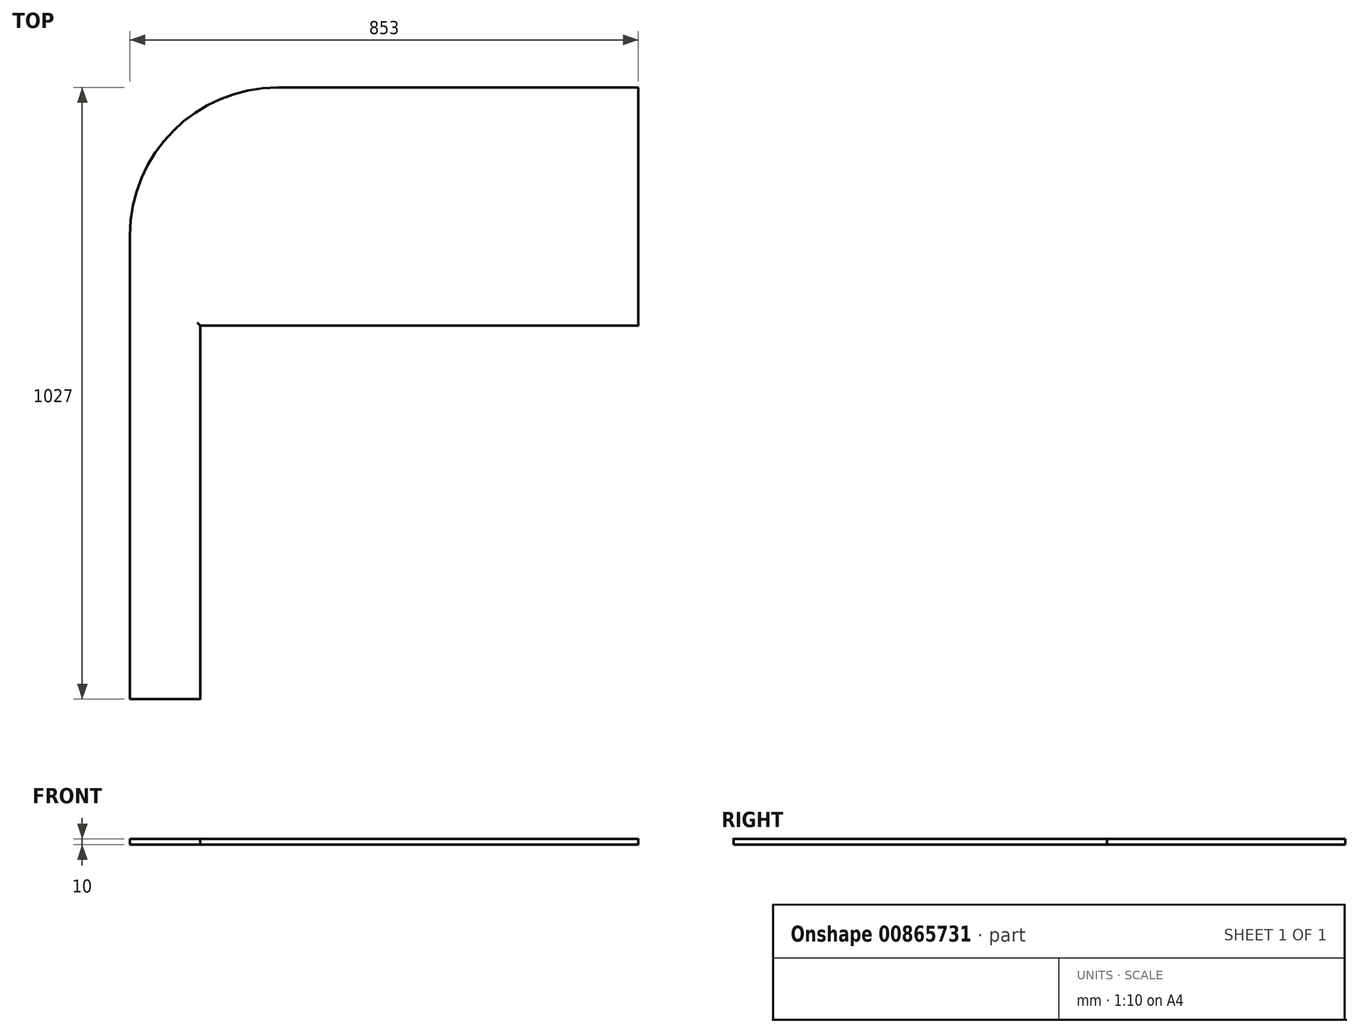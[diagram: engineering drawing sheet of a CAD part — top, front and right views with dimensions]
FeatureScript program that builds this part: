
annotation { "Feature Type Name" : "Feature", "Feature Type Description" : "" }
export const myFeature = defineFeature(function(context is Context, id is Id, definition is map)
    precondition{}
    {
        {
            var Q0;
            Q0=qCreatedBy(makeId("Top.planeOp"),FACE);
            var sketch = newSketch(context, id + "F0", { "sketchPlane" : qUnion([Q0])});
            skLineSegment(sketch, "E0", {"start": v(-248, 0) * mm, "end": v(-248, -779) * mm});
            skLineSegment(sketch, "E1", {"start": v(0, 248) * mm, "end": v(605, 248) * mm});
            skArc(sketch, "E2", {"start": v(0, 248) * mm, "mid": v(-175.36, 175.36) * mm, "end": v(-248, 0) * mm});
            skLineSegment(sketch, "E3", {"start": v(-248, -779) * mm, "end": v(-130, -779) * mm});
            skLineSegment(sketch, "E4", {"start": v(605, 248) * mm, "end": v(605, -152) * mm});
            skLineSegment(sketch, "E5", {"start": v(605, -152) * mm, "end": v(-130, -152) * mm});
            skLineSegment(sketch, "E6", {"start": v(-130, -152) * mm, "end": v(-130, -779) * mm});
            skSolve(sketch);
        }
        {
            var Q0;
            Q0 = qSketchRegion(id + "F0", true);
            extrude(context, id + "F1", {"entities" : qUnion([Q0]), "depth" : 10 * mm, "offsetDistance" : 25 * mm});
        }
        {
            var Q0;
            Q0=makeQuery(id+"F1.opExtrude","CAP_EDGE",EDGE,{"disambiguationData":[OSD([sQuery(id+"F0.wireOp",EDGE,"E5")])],"isStart":false});
            var Q1;
            Q1=makeQuery(id+"F1.opExtrude","CAP_EDGE",EDGE,{"disambiguationData":[OSD([sQuery(id+"F0.wireOp",EDGE,"E6")])],"isStart":false});
            fillet(context, id + "F2", {"entities" : qUnion([Q0, Q1]), "radius" : 5 * mm, "tangentPropagation" : true, "allowEdgeOverflow" : false});
        }
    });
